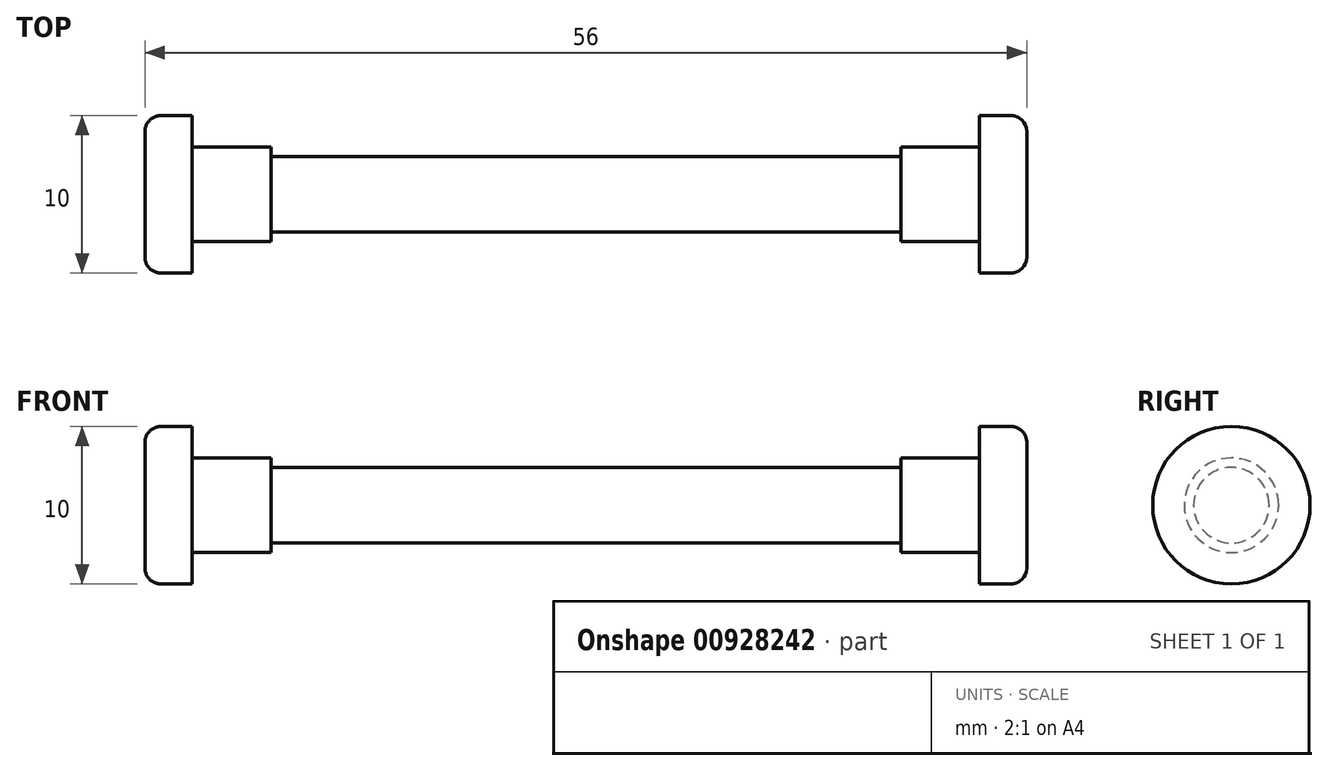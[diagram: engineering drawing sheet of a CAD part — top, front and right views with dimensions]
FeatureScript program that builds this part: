
annotation { "Feature Type Name" : "Feature", "Feature Type Description" : "" }
export const myFeature = defineFeature(function(context is Context, id is Id, definition is map)
    precondition{}
    {
        {
            var Q0;
            Q0=qCreatedBy(makeId("Top.planeOp"),FACE);
            var sketch = newSketch(context, id + "F0", { "sketchPlane" : qUnion([Q0])});
            skLineSegment(sketch, "E0", {"start": v(-68.56, 0) * mm, "end": v(70.82, 0) * mm, "construction": true});
            skLineSegment(sketch, "E1", {"start": v(-28, 0) * mm, "end": v(28, 0) * mm});
            skLineSegment(sketch, "E2", {"start": v(25, 3) * mm, "end": v(20, 3) * mm});
            skLineSegment(sketch, "E3", {"start": v(20, 3) * mm, "end": v(20, 2.4) * mm});
            skLineSegment(sketch, "E4", {"start": v(20, 2.4) * mm, "end": v(-20, 2.4) * mm});
            skLineSegment(sketch, "E5", {"start": v(-28, 0) * mm, "end": v(-28, 4) * mm});
            skLineSegment(sketch, "E6", {"start": v(-25, 3) * mm, "end": v(-20, 3) * mm});
            skLineSegment(sketch, "E7", {"start": v(-20, 3) * mm, "end": v(-20, 2.4) * mm});
            skLineSegment(sketch, "E8", {"start": v(25, 3) * mm, "end": v(25, 5) * mm});
            skLineSegment(sketch, "E9", {"start": v(25, 5) * mm, "end": v(27, 5) * mm});
            skLineSegment(sketch, "E10", {"start": v(28, 4) * mm, "end": v(28, 0) * mm});
            skLineSegment(sketch, "E11", {"start": v(-27, 5) * mm, "end": v(-25, 5) * mm});
            skLineSegment(sketch, "E12", {"start": v(-25, 5) * mm, "end": v(-25, 3) * mm});
            skPoint(sketch, "E13.visualSharp", {"position": v(-28, 5) * mm});
            skArc(sketch, "E13.filletArc", {"start": v(-27, 5) * mm, "mid": v(-27.7, 4.7) * mm, "end": v(-28, 4) * mm});
            skPoint(sketch, "E14.visualSharp", {"position": v(28, 5) * mm});
            skArc(sketch, "E14.filletArc", {"start": v(28, 4) * mm, "mid": v(27.7, 4.7) * mm, "end": v(27, 5) * mm});
            skSolve(sketch);
        }
        {
            var Q0;
            Q0=makeQuery(id+"F0.imprint","IMPRINT",FACE,{"disambiguationData":[TD([[makeQuery(id+"F0.imprint","IMPRINT",EDGE,{"derivedFrom":sQuery(id+"F0.wireOp",EDGE,"E1")}),1.0]])]});
            var Q1;
            Q1=sQuery(id+"F0.wireOp",EDGE,"E0");
            revolve(context, id + "F1", {"surfaceOperationType" : NewSurfaceOperationType.NEW, "entities" : qUnion([Q0]), "axis" : qUnion([Q1]), "revolveType" : RevolveType.FULL});
        }
    });
